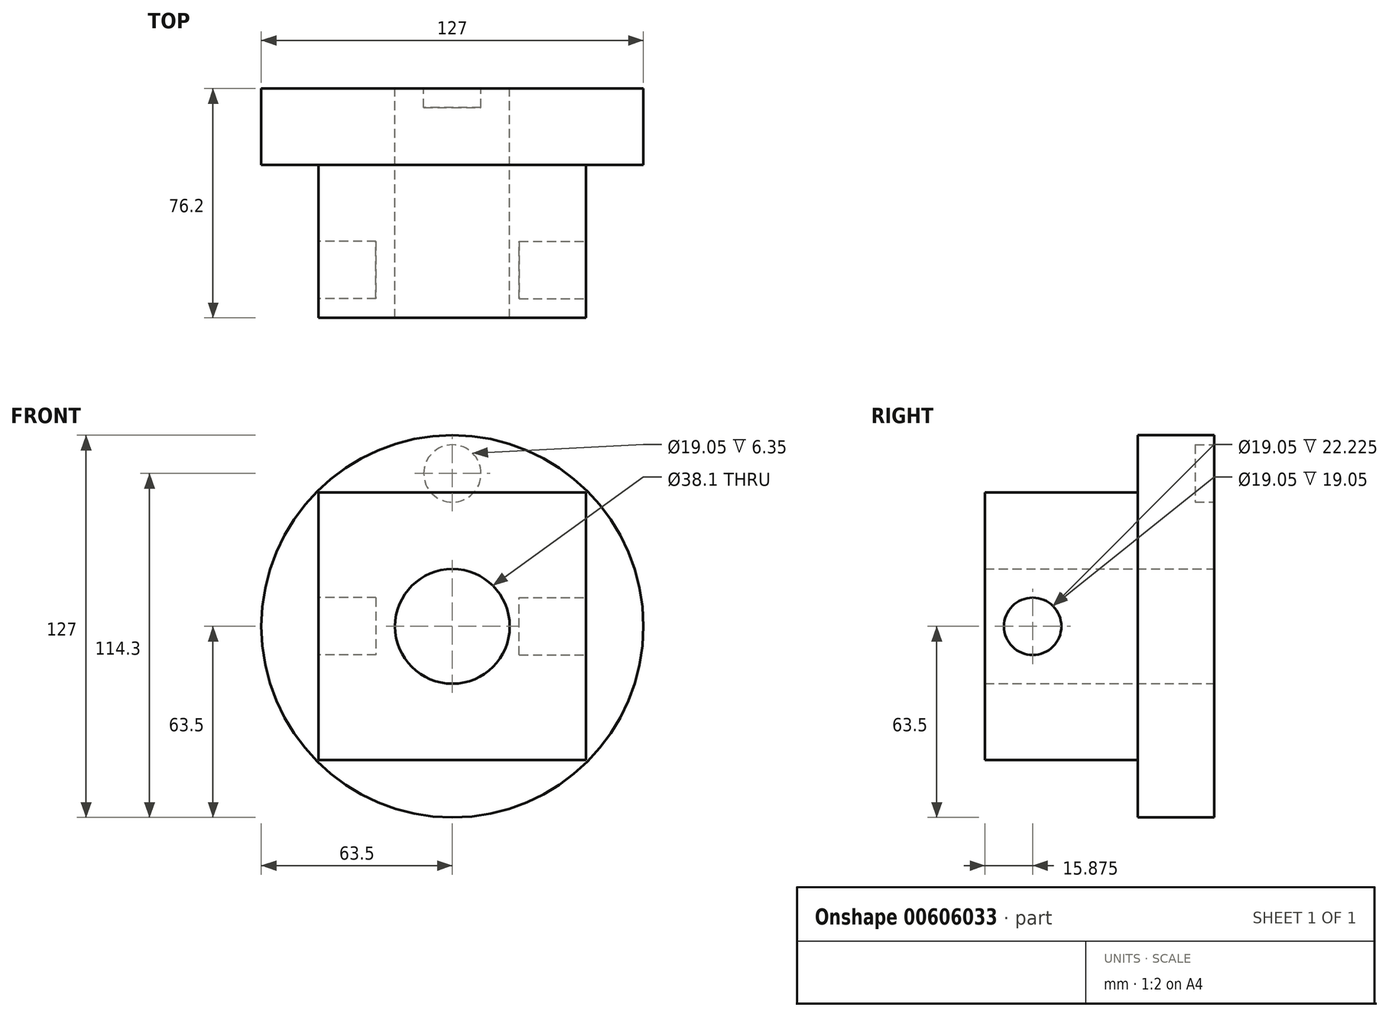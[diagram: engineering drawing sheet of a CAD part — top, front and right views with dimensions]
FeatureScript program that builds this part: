
annotation { "Feature Type Name" : "Feature", "Feature Type Description" : "" }
export const myFeature = defineFeature(function(context is Context, id is Id, definition is map)
    precondition{}
    {
        {
            var Q0;
            Q0=qCreatedBy(makeId("Front.planeOp"),FACE);
            var sketch = newSketch(context, id + "F0", { "sketchPlane" : qUnion([Q0])});
            skCircle(sketch, "E0", {"center": v(0, 0) * mm, "radius": 63.5 * mm});
            skSolve(sketch);
        }
        {
            var Q0;
            Q0 = qSketchRegion(id + "F0", true);
            extrude(context, id + "F1", {"entities" : qUnion([Q0]), "depth" : 25.4 * mm, "offsetDistance" : 25.4 * mm});
        }
        {
            var Q0;
            Q0=makeQuery(id+"F1.opExtrude","CAP_FACE",FACE,{"disambiguationData":[OSD([sQuery(id+"F0.wireOp",EDGE,"E0")])],"isStart":true});
            var sketch = newSketch(context, id + "F2", { "sketchPlane" : qUnion([Q0])});
            skCircle(sketch, "E1", {"center": v(0, 50.8) * mm, "radius": 9.53 * mm});
            skSolve(sketch);
        }
        {
            var Q0;
            Q0 = qSketchRegion(id + "F2", true);
            extrude(context, id + "F3", {"entities" : qUnion([Q0]), "operationType" : NewBodyOperationType.REMOVE, "oppositeDirection" : true, "depth" : 6.35 * mm, "offsetDistance" : 25.4 * mm});
        }
        {
            var Q0;
            Q0=makeQuery(id+"F1.opExtrude","CAP_FACE",FACE,{"disambiguationData":[OSD([sQuery(id+"F0.wireOp",EDGE,"E0")])],"isStart":true});
            var sketch = newSketch(context, id + "F4", { "sketchPlane" : qUnion([Q0])});
            skCircle(sketch, "E2", {"center": v(0, 0) * mm, "radius": 19.05 * mm});
            skSolve(sketch);
        }
        {
            var Q0;
            Q0=makeQuery(id+"F1.opExtrude","CAP_FACE",FACE,{"disambiguationData":[OSD([sQuery(id+"F0.wireOp",EDGE,"E0")])],"isStart":false});
            var sketch = newSketch(context, id + "F5", { "sketchPlane" : qUnion([Q0])});
            skLineSegment(sketch, "E3.bottom", {"start": v(44.45, 44.45) * mm, "end": v(-44.45, 44.45) * mm});
            skLineSegment(sketch, "E3.top", {"start": v(44.45, -44.45) * mm, "end": v(-44.45, -44.45) * mm});
            skLineSegment(sketch, "E3.left", {"start": v(44.45, 44.45) * mm, "end": v(44.45, -44.45) * mm});
            skLineSegment(sketch, "E3.right", {"start": v(-44.45, 44.45) * mm, "end": v(-44.45, -44.45) * mm});
            skPoint(sketch, "E3.middle", {"position": v(0, 0) * mm});
            skSolve(sketch);
        }
        {
            var Q0;
            Q0 = qSketchRegion(id + "F5", true);
            extrude(context, id + "F6", {"entities" : qUnion([Q0]), "operationType" : NewBodyOperationType.ADD, "depth" : 50.8 * mm, "offsetDistance" : 25.4 * mm});
        }
        {
            var Q0;
            Q0 = qSketchRegion(id + "F4", true);
            extrude(context, id + "F7", {"entities" : qUnion([Q0]), "operationType" : NewBodyOperationType.REMOVE, "oppositeDirection" : true, "depth" : 101.6 * mm, "offsetDistance" : 25.4 * mm});
        }
        {
            var Q0;
            Q0=makeQuery(id+"F6.opExtrude","SWEPT_FACE",FACE,{"disambiguationData":[OSD([sQuery(id+"F5.wireOp",EDGE,"E3.left")])]});
            var sketch = newSketch(context, id + "F8", { "sketchPlane" : qUnion([Q0])});
            skCircle(sketch, "E4", {"center": v(-60.33, 0) * mm, "radius": 9.53 * mm});
            skSolve(sketch);
        }
        {
            var Q0;
            Q0=makeQuery(id+"F8.imprint","IMPRINT",FACE,{"disambiguationData":[TD([[makeQuery(id+"F8.imprint","IMPRINT",EDGE,{"derivedFrom":sQuery(id+"F8.wireOp",EDGE,"E4")}),1.0]])]});
            extrude(context, id + "F9", {"entities" : qUnion([Q0]), "operationType" : NewBodyOperationType.REMOVE, "oppositeDirection" : true, "depth" : 22.22 * mm, "offsetDistance" : 25.4 * mm});
        }
        {
            var Q0;
            Q0=makeQuery(id+"F6.opExtrude","SWEPT_FACE",FACE,{"disambiguationData":[OSD([sQuery(id+"F5.wireOp",EDGE,"E3.right")])]});
            var sketch = newSketch(context, id + "F10", { "sketchPlane" : qUnion([Q0])});
            skCircle(sketch, "E5", {"center": v(60.33, 0) * mm, "radius": 9.53 * mm});
            skSolve(sketch);
        }
        {
            var Q0;
            Q0=makeQuery(id+"F10.imprint","IMPRINT",FACE,{"disambiguationData":[TD([[makeQuery(id+"F10.imprint","IMPRINT",EDGE,{"derivedFrom":sQuery(id+"F10.wireOp",EDGE,"E5")}),1.0]])]});
            extrude(context, id + "F11", {"entities" : qUnion([Q0]), "operationType" : NewBodyOperationType.REMOVE, "oppositeDirection" : true, "depth" : 19.05 * mm, "offsetDistance" : 25.4 * mm});
        }
    });
